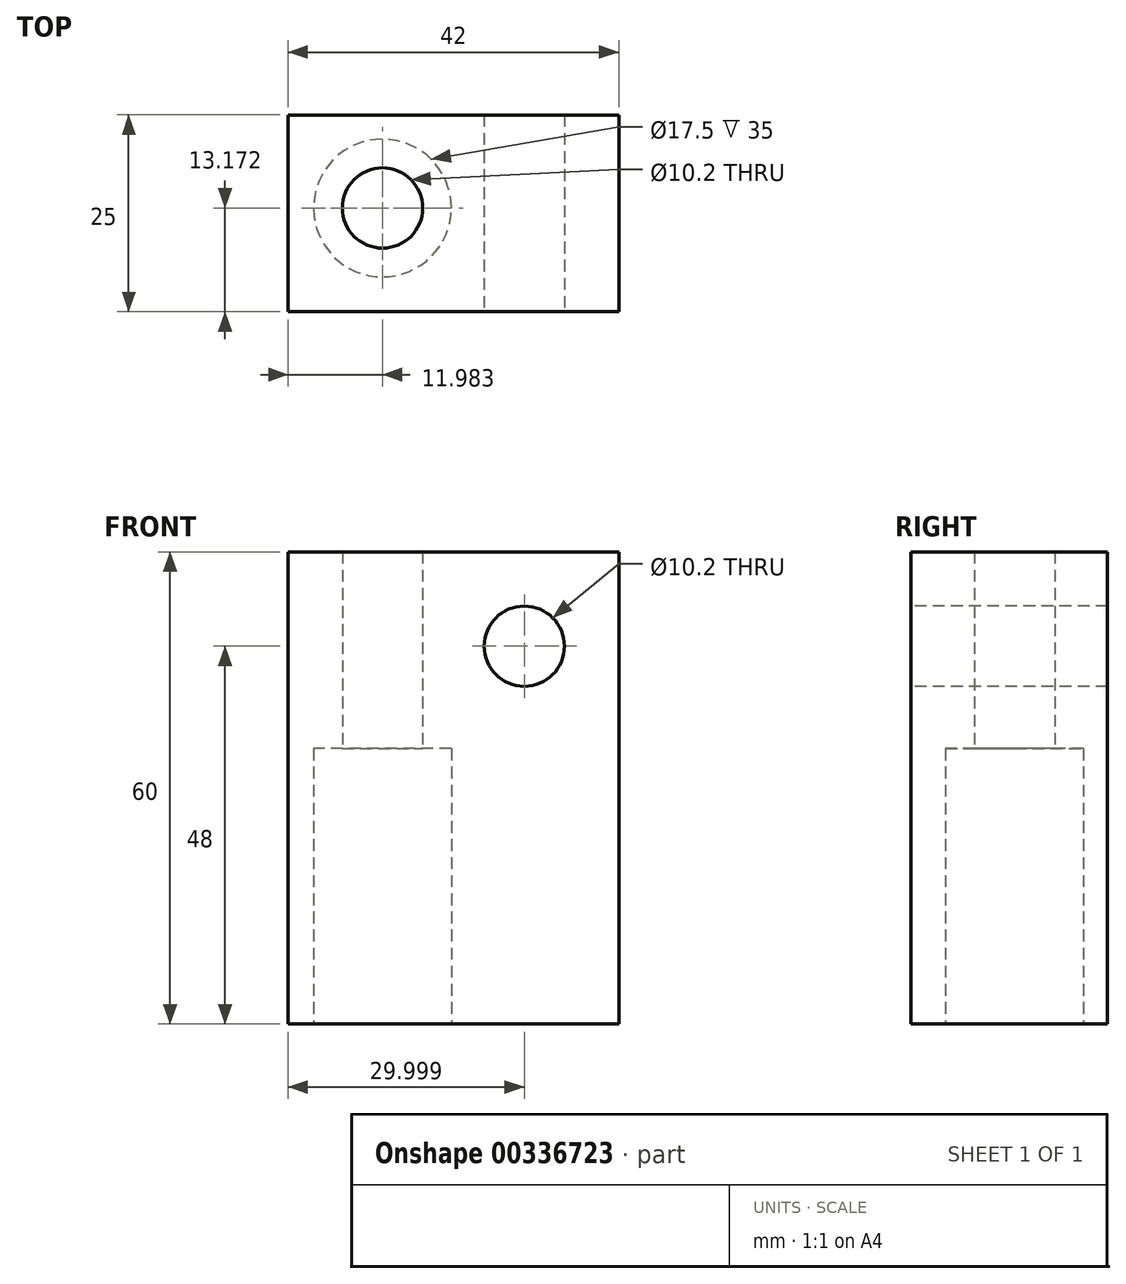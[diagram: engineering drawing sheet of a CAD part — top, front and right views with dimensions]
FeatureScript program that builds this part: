
annotation { "Feature Type Name" : "Feature", "Feature Type Description" : "" }
export const myFeature = defineFeature(function(context is Context, id is Id, definition is map)
    precondition{}
    {
        {
            var Q0;
            Q0=qCreatedBy(makeId("Top.planeOp"),FACE);
            var sketch = newSketch(context, id + "F0", { "sketchPlane" : qUnion([Q0])});
            skLineSegment(sketch, "E0.bottom", {"start": v(-35.43, -18.98) * mm, "end": v(6.57, -18.98) * mm});
            skLineSegment(sketch, "E0.top", {"start": v(-35.43, 6.02) * mm, "end": v(6.57, 6.02) * mm});
            skLineSegment(sketch, "E0.left", {"start": v(-35.43, -18.98) * mm, "end": v(-35.43, 6.02) * mm});
            skLineSegment(sketch, "E0.right", {"start": v(6.57, -18.98) * mm, "end": v(6.57, 6.02) * mm});
            skSolve(sketch);
        }
        {
            var Q0;
            Q0 = qSketchRegion(id + "F0", true);
            extrude(context, id + "F1", {"entities" : qUnion([Q0]), "depth" : 60 * mm});
        }
        {
            var Q0;
            Q0=makeQuery(id+"F1.opExtrude","SWEPT_FACE",FACE,{"disambiguationData":[OSD([sQuery(id+"F0.wireOp",EDGE,"E0.bottom")])]});
            var sketch = newSketch(context, id + "F2", { "sketchPlane" : qUnion([Q0])});
            skLineSegment(sketch, "E1", {"start": v(6.57, 60) * mm, "end": v(-5.43, 60) * mm});
            skLineSegment(sketch, "E2", {"start": v(6.57, 60) * mm, "end": v(6.57, 48) * mm});
            skCircle(sketch, "E3", {"center": v(-5.43, 48) * mm, "radius": 5.1 * mm});
            skSolve(sketch);
        }
        {
            var Q0;
            Q0=qCreatedBy(makeId("Top.planeOp"),FACE);
            var sketch = newSketch(context, id + "F3", { "sketchPlane" : qUnion([Q0])});
            skCircle(sketch, "E4", {"center": v(-23.45, -5.8) * mm, "radius": 8.75 * mm});
            skPoint(sketch, "E5.end.orphan", {"position": v(-35.45, -5.8) * mm});
            skSolve(sketch);
        }
        {
            var Q0;
            Q0 = qSketchRegion(id + "F3", true);
            extrude(context, id + "F4", {"entities" : qUnion([Q0]), "operationType" : NewBodyOperationType.REMOVE, "depth" : 35 * mm});
        }
        {
            var Q0;
            Q0 = qSketchRegion(id + "F2", true);
            extrude(context, id + "F5", {"entities" : qUnion([Q0]), "operationType" : NewBodyOperationType.REMOVE, "endBound" : BoundingType.THROUGH_ALL, "oppositeDirection" : true, "depth" : 25 * mm});
        }
        {
            var Q0;
            Q0=makeQuery(id+"F4.boolean.opBoolean","COPY",FACE,{"derivedFrom":makeQuery(id+"F4.opExtrude","CAP_FACE",FACE,{"disambiguationData":[OSD([sQuery(id+"F3.wireOp",EDGE,"E4")])],"isStart":false})});
            var sketch = newSketch(context, id + "F6", { "sketchPlane" : qUnion([Q0])});
            skCircle(sketch, "E6", {"center": v(-23.45, 5.8) * mm, "radius": 5.1 * mm});
            skSolve(sketch);
        }
        {
            var Q0;
            Q0=makeQuery(id+"F6.imprint","IMPRINT",FACE,{"disambiguationData":[TD([[makeQuery(id+"F6.imprint","IMPRINT",EDGE,{"derivedFrom":sQuery(id+"F6.wireOp",EDGE,"E6")}),1.0]])]});
            extrude(context, id + "F7", {"entities" : qUnion([Q0]), "operationType" : NewBodyOperationType.REMOVE, "oppositeDirection" : true, "depth" : 35 * mm});
        }
    });
